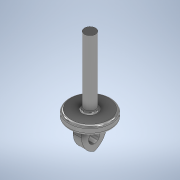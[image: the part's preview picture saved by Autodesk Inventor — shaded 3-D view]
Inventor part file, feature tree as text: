
AUTODESK INVENTOR PART (.ipt)
format: ipt  version: 2020 (Build 240168000, 168)  size: 160,768 bytes
history: native  units: mm
features: fillet x2, sketch x1, revolve x1, extrude x1
ambient origin geometry x8: Origin, YZ Plane, XZ Plane, XY Plane, X Axis, Y Axis, Z Axis, Center Point
bodies: Solid1 (feature_tree)
feature tree (5):
  sketch  "Sketch1"  dims[d0=9.85mm d1=120.0mm d2=27.65mm d3=15.0mm d4=22.5mm d5=15.0mm d6=22.5mm d9=90.0deg d10=15.0mm d11=0.0mm d12=4.0mm d13=4.0mm d14=33.75mm d15=33.75mm d16=20.0mm d17=25.0mm]
  revolve  "Revolution1"  [1 undecoded]
  extrude  "Extrusion1"  Depth=33.75mm
  fillet  "Fillet1"  Radius=15.0mm
  fillet  "Fillet2"  Radius=22.5mm
note: 1 required parameter value undecoded (feature->parameter linkage not recoverable at this tier; creation-order binding heuristic only, values carry confidence <= 0.55)
